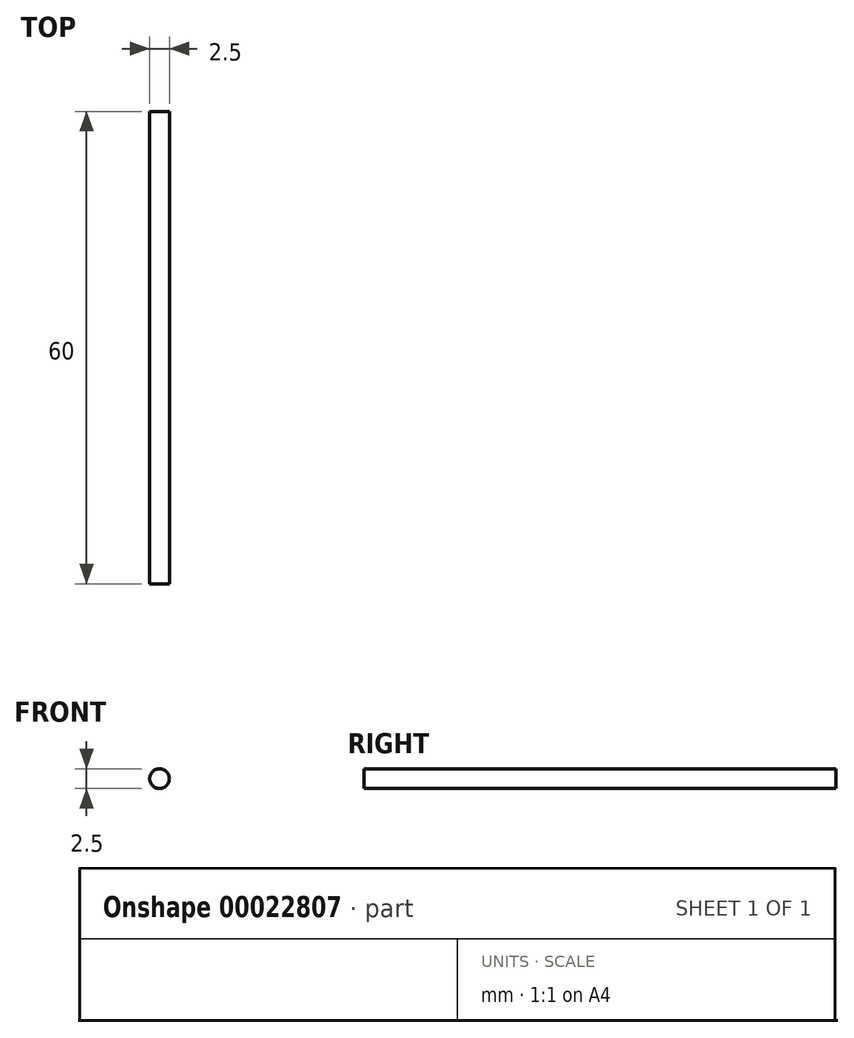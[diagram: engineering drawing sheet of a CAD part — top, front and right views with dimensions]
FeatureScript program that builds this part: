
annotation { "Feature Type Name" : "Feature", "Feature Type Description" : "" }
export const myFeature = defineFeature(function(context is Context, id is Id, definition is map)
    precondition{}
    {
        {
            var Q0;
            Q0=qCreatedBy(makeId("Front.planeOp"),FACE);
            var sketch = newSketch(context, id + "F0", { "sketchPlane" : qUnion([Q0])});
            skCircle(sketch, "E0", {"center": v(-35.44, 12.29) * mm, "radius": 1.25 * mm});
            skSolve(sketch);
        }
        {
            var Q0;
            Q0=makeQuery(id+"F0.imprint","IMPRINT",FACE,{"disambiguationData":[TD([[makeQuery(id+"F0.imprint","IMPRINT",EDGE,{"derivedFrom":sQuery(id+"F0.wireOp",EDGE,"E0")}),1.0]])]});
            extrude(context, id + "F1", {"entities" : qUnion([Q0]), "depth" : 60 * mm});
        }
    });
